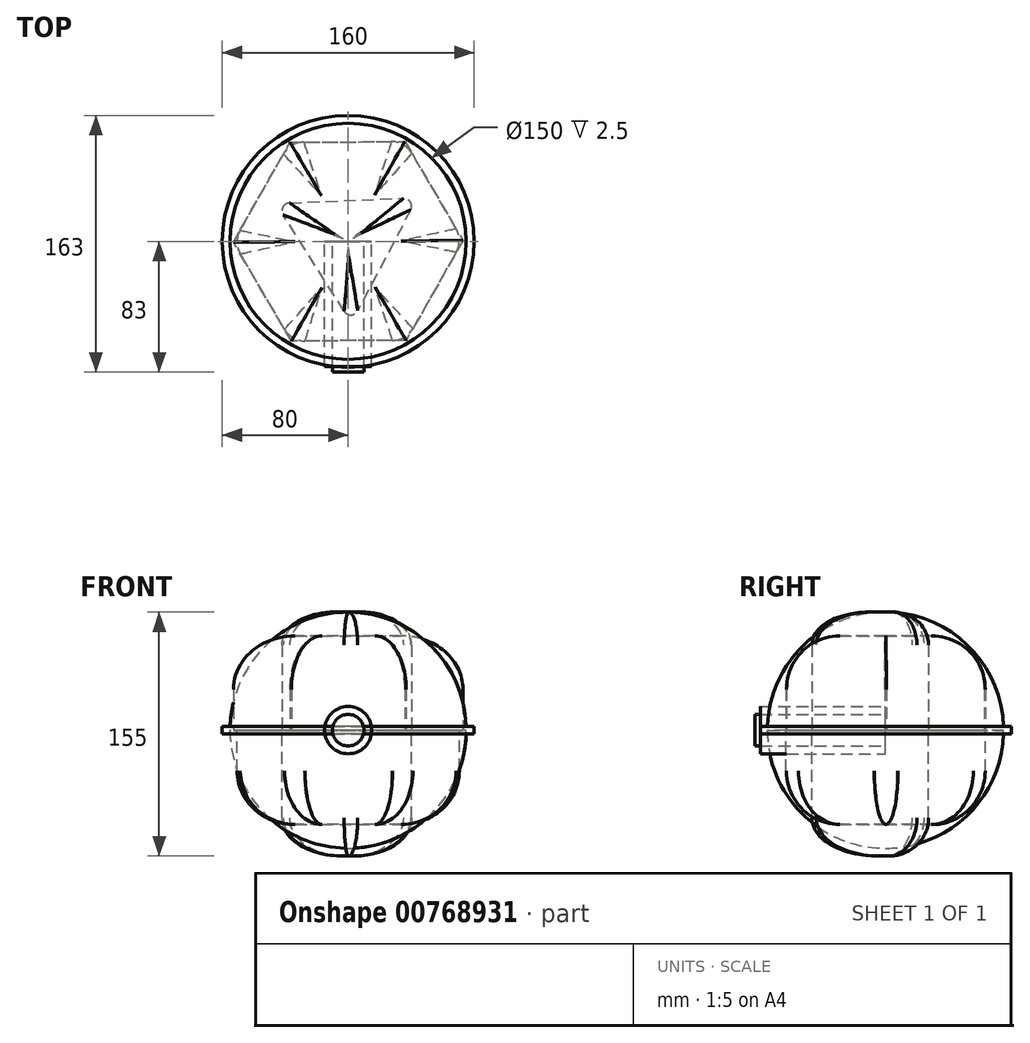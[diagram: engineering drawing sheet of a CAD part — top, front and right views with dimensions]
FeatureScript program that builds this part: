
annotation { "Feature Type Name" : "Feature", "Feature Type Description" : "" }
export const myFeature = defineFeature(function(context is Context, id is Id, definition is map)
    precondition{}
    {
        {
            var Q0;
            Q0=qCreatedBy(makeId("Top.planeOp"),FACE);
            var sketch = newSketch(context, id + "F0", { "sketchPlane" : qUnion([Q0])});
            skCircle(sketch, "E0", {"center": v(0, 0) * mm, "radius": 75 * mm});
            skSolve(sketch);
        }
        {
            var Q0;
            Q0=makeQuery(id+"F0.imprint","IMPRINT",FACE,{"disambiguationData":[TD([[makeQuery(id+"F0.imprint","IMPRINT",EDGE,{"derivedFrom":sQuery(id+"F0.wireOp",EDGE,"E0")}),1.0]])]});
            extrude(context, id + "F1", {"entities" : qUnion([Q0]), "depth" : 75 * mm, "offsetDistance" : 25 * mm});
        }
        {
            var Q0;
            Q0=makeQuery(id+"F1.opExtrude","CAP_FACE",FACE,{"disambiguationData":[OSD([sQuery(id+"F0.wireOp",EDGE,"E0")])],"isStart":true});
            extrude(context, id + "F2", {"entities" : qUnion([Q0]), "operationType" : NewBodyOperationType.ADD, "depth" : 75 * mm, "offsetDistance" : 25 * mm});
        }
        {
            var Q0;
            Q0=makeQuery(id+"F1.opExtrude","CAP_FACE",FACE,{"disambiguationData":[OSD([sQuery(id+"F0.wireOp",EDGE,"E0")])],"isStart":false});
            fillet(context, id + "F3", {"entities" : qUnion([Q0]), "radius" : 75 * mm, "tangentPropagation" : true, "allowEdgeOverflow" : false});
        }
        {
            var Q0;
            Q0=makeQuery(id+"F2.opExtrude","CAP_FACE",FACE,{"disambiguationData":[OSD([sQuery(id+"F0.wireOp",EDGE,"E0")])],"isStart":false});
            fillet(context, id + "F4", {"entities" : qUnion([Q0]), "radius" : 75 * mm, "tangentPropagation" : true, "allowEdgeOverflow" : false});
        }
        {
            var Q0;
            Q0=qCreatedBy(makeId("Top.planeOp"),FACE);
            var sketch = newSketch(context, id + "F5", { "sketchPlane" : qUnion([Q0])});
            skCircle(sketch, "E1", {"center": v(0, 0) * mm, "radius": 80 * mm});
            skSolve(sketch);
        }
        {
            var Q0;
            Q0=makeQuery(id+"F5.imprint","IMPRINT",FACE,{"disambiguationData":[TD([[makeQuery(id+"F5.imprint","IMPRINT",EDGE,{"derivedFrom":sQuery(id+"F5.wireOp",EDGE,"E1")}),1.0]])]});
            extrude(context, id + "F6", {"entities" : qUnion([Q0]), "operationType" : NewBodyOperationType.ADD, "depth" : 2.5 * mm, "offsetDistance" : 25 * mm});
        }
        {
            var Q0;
            Q0=makeQuery(id+"F6.opExtrude","CAP_FACE",FACE,{"disambiguationData":[OSD([sQuery(id+"F5.wireOp",EDGE,"E1")])],"isStart":true});
            extrude(context, id + "F7", {"entities" : qUnion([Q0]), "operationType" : NewBodyOperationType.ADD, "depth" : 2.5 * mm, "offsetDistance" : 25 * mm});
        }
        {
            var Q0;
            Q0=qCreatedBy(makeId("Front.planeOp"),FACE);
            var sketch = newSketch(context, id + "F8", { "sketchPlane" : qUnion([Q0])});
            skCircle(sketch, "E2", {"center": v(0, 0) * mm, "radius": 15 * mm});
            skSolve(sketch);
        }
        {
            var Q0;
            Q0=sQuery(id+"F8.wireOp",EDGE,"E2");
            extrude(context, id + "F9", {"bodyType" : ToolBodyType.SURFACE, "surfaceEntities" : qUnion([Q0]), "depth" : 78.5 * mm, "offsetDistance" : 25 * mm});
        }
        {
            var Q0;
            Q0=qCreatedBy(makeId("Front.planeOp"),FACE);
            var sketch = newSketch(context, id + "F10", { "sketchPlane" : qUnion([Q0])});
            skCircle(sketch, "E3", {"center": v(0, 0) * mm, "radius": 10 * mm});
            skSolve(sketch);
        }
        {
            var Q0;
            Q0=sQuery(id+"F10.wireOp",EDGE,"E3");
            extrude(context, id + "F11", {"bodyType" : ToolBodyType.SURFACE, "surfaceEntities" : qUnion([Q0]), "depth" : 83 * mm, "offsetDistance" : 25 * mm});
        }
        {
            var Q0;
            Q0 = qSketchRegion(id + "F10", true);
            extrude(context, id + "F12", {"entities" : qUnion([Q0]), "depth" : 83 * mm, "offsetDistance" : 25 * mm});
        }
        {
            var Q0;
            Q0 = qSketchRegion(id + "F8", true);
            extrude(context, id + "F13", {"entities" : qUnion([Q0]), "depth" : 79.5 * mm, "offsetDistance" : 25 * mm});
        }
        {
            var Q0;
            Q0=qCreatedBy(makeId("Top.planeOp"),FACE);
            var sketch = newSketch(context, id + "F14", { "sketchPlane" : qUnion([Q0])});
            skCircle(sketch, "E4.cCircle", {"center": v(0, 0) * mm, "radius": 25.89 * mm, "construction": true});
            skLineSegment(sketch, "E4.0", {"start": v(43.76, 27.68) * mm, "end": v(2.1, -51.73) * mm});
            skLineSegment(sketch, "E4.1", {"start": v(2.1, -51.73) * mm, "end": v(-45.85, 24.06) * mm});
            skLineSegment(sketch, "E4.2", {"start": v(-45.85, 24.06) * mm, "end": v(43.76, 27.68) * mm});
            skPoint(sketch, "E4.0.midPoint", {"position": v(22.92, -12.03) * mm});
            skSolve(sketch);
        }
        {
            var Q0;
            Q0 = qSketchRegion(id + "F14", true);
            extrude(context, id + "F15", {"entities" : qUnion([Q0]), "depth" : 75 * mm, "offsetDistance" : 25 * mm});
        }
        {
            var Q0;
            Q0=makeQuery(id+"F15.opExtrude","SWEPT_EDGE",EDGE,{"disambiguationData":[OSD([sQuery(id+"F14.wireOp",EDGE,"E4.0"),sQuery(id+"F14.wireOp",EDGE,"E4.1")])]});
            var Q1;
            Q1=makeQuery(id+"F15.opExtrude","SWEPT_EDGE",EDGE,{"disambiguationData":[OSD([sQuery(id+"F14.wireOp",EDGE,"E4.0"),sQuery(id+"F14.wireOp",EDGE,"E4.2")])]});
            var Q2;
            Q2=makeQuery(id+"F15.opExtrude","SWEPT_EDGE",EDGE,{"disambiguationData":[OSD([sQuery(id+"F14.wireOp",EDGE,"E4.1"),sQuery(id+"F14.wireOp",EDGE,"E4.2")])]});
            fillet(context, id + "F16", {"entities" : qUnion([Q0, Q1, Q2]), "radius" : 5 * mm, "tangentPropagation" : true, "allowEdgeOverflow" : false});
        }
        {
            var Q0;
            Q0=makeQuery(id+"F15.opExtrude","CAP_FACE",FACE,{"disambiguationData":[OSD([sQuery(id+"F14.wireOp",EDGE,"E4.0"),sQuery(id+"F14.wireOp",EDGE,"E4.1"),sQuery(id+"F14.wireOp",EDGE,"E4.2")])],"isStart":false});
            fillet(context, id + "F17", {"entities" : qUnion([Q0]), "radius" : 21 * mm, "tangentPropagation" : true, "allowEdgeOverflow" : false});
        }
        {
            var Q0;
            Q0 = qSketchRegion(id + "F14", true);
            extrude(context, id + "F18", {"entities" : qUnion([Q0]), "oppositeDirection" : true, "depth" : 80 * mm, "offsetDistance" : 25 * mm});
        }
        {
            var Q0;
            Q0=makeQuery(id+"F18.opExtrude","SWEPT_EDGE",EDGE,{"disambiguationData":[OSD([sQuery(id+"F14.wireOp",EDGE,"E4.1"),sQuery(id+"F14.wireOp",EDGE,"E4.2")])]});
            var Q1;
            Q1=makeQuery(id+"F18.opExtrude","SWEPT_EDGE",EDGE,{"disambiguationData":[OSD([sQuery(id+"F14.wireOp",EDGE,"E4.0"),sQuery(id+"F14.wireOp",EDGE,"E4.2")])]});
            var Q2;
            Q2=makeQuery(id+"F18.opExtrude","SWEPT_EDGE",EDGE,{"disambiguationData":[OSD([sQuery(id+"F14.wireOp",EDGE,"E4.0"),sQuery(id+"F14.wireOp",EDGE,"E4.1")])]});
            fillet(context, id + "F19", {"entities" : qUnion([Q0, Q1, Q2]), "radius" : 5 * mm, "tangentPropagation" : true, "allowEdgeOverflow" : false});
        }
        {
            var Q0;
            Q0=makeQuery(id+"F18.opExtrude","CAP_FACE",FACE,{"disambiguationData":[OSD([sQuery(id+"F14.wireOp",EDGE,"E4.0"),sQuery(id+"F14.wireOp",EDGE,"E4.1"),sQuery(id+"F14.wireOp",EDGE,"E4.2")])],"isStart":false});
            fillet(context, id + "F20", {"entities" : qUnion([Q0]), "radius" : 24.14 * mm, "tangentPropagation" : true, "allowEdgeOverflow" : false});
        }
        {
            var Q0;
            Q0=qCreatedBy(makeId("Top.planeOp"),FACE);
            var sketch = newSketch(context, id + "F21", { "sketchPlane" : qUnion([Q0])});
            skCircle(sketch, "E5.cCircle", {"center": v(0, 0) * mm, "radius": 63.14 * mm, "construction": true});
            skLineSegment(sketch, "E5.0", {"start": v(36.04, 63.37) * mm, "end": v(72.9, 0.48) * mm});
            skLineSegment(sketch, "E5.1", {"start": v(72.9, 0.48) * mm, "end": v(36.86, -62.9) * mm});
            skLineSegment(sketch, "E5.2", {"start": v(36.86, -62.9) * mm, "end": v(-36.04, -63.37) * mm});
            skLineSegment(sketch, "E5.3", {"start": v(-36.04, -63.37) * mm, "end": v(-72.9, -0.48) * mm});
            skLineSegment(sketch, "E5.4", {"start": v(-72.9, -0.48) * mm, "end": v(-36.86, 62.9) * mm});
            skLineSegment(sketch, "E5.5", {"start": v(-36.86, 62.9) * mm, "end": v(36.04, 63.37) * mm});
            skPoint(sketch, "E5.0.midPoint", {"position": v(54.47, 31.93) * mm});
            skSolve(sketch);
        }
        {
            var Q0;
            Q0 = qSketchRegion(id + "F21", true);
            extrude(context, id + "F22", {"entities" : qUnion([Q0]), "oppositeDirection" : true, "depth" : 60 * mm, "offsetDistance" : 25 * mm});
        }
        {
            var Q0;
            Q0 = qSketchRegion(id + "F21", true);
            extrude(context, id + "F23", {"entities" : qUnion([Q0]), "depth" : 60 * mm, "offsetDistance" : 25 * mm});
        }
        {
            var Q0;
            Q0=makeQuery(id+"F22.opExtrude","SWEPT_EDGE",EDGE,{"disambiguationData":[OSD([sQuery(id+"F21.wireOp",EDGE,"E5.1"),sQuery(id+"F21.wireOp",EDGE,"E5.2")])]});
            var Q1;
            Q1=makeQuery(id+"F22.opExtrude","SWEPT_EDGE",EDGE,{"disambiguationData":[OSD([sQuery(id+"F21.wireOp",EDGE,"E5.0"),sQuery(id+"F21.wireOp",EDGE,"E5.1")])]});
            var Q2;
            Q2=makeQuery(id+"F22.opExtrude","SWEPT_EDGE",EDGE,{"disambiguationData":[OSD([sQuery(id+"F21.wireOp",EDGE,"E5.4"),sQuery(id+"F21.wireOp",EDGE,"E5.5")])]});
            var Q3;
            Q3=makeQuery(id+"F22.opExtrude","SWEPT_EDGE",EDGE,{"disambiguationData":[OSD([sQuery(id+"F21.wireOp",EDGE,"E5.3"),sQuery(id+"F21.wireOp",EDGE,"E5.4")])]});
            var Q4;
            Q4=makeQuery(id+"F22.opExtrude","SWEPT_EDGE",EDGE,{"disambiguationData":[OSD([sQuery(id+"F21.wireOp",EDGE,"E5.2"),sQuery(id+"F21.wireOp",EDGE,"E5.3")])]});
            var Q5;
            Q5=makeQuery(id+"F22.opExtrude","SWEPT_EDGE",EDGE,{"disambiguationData":[OSD([sQuery(id+"F21.wireOp",EDGE,"E5.0"),sQuery(id+"F21.wireOp",EDGE,"E5.5")])]});
            fillet(context, id + "F24", {"entities" : qUnion([Q0, Q1, Q2, Q3, Q4, Q5]), "radius" : 15 * mm, "tangentPropagation" : true, "allowEdgeOverflow" : false});
        }
        {
            var Q0;
            Q0=makeQuery(id+"F22.opExtrude","CAP_FACE",FACE,{"disambiguationData":[OSD([sQuery(id+"F21.wireOp",EDGE,"E5.0"),sQuery(id+"F21.wireOp",EDGE,"E5.1"),sQuery(id+"F21.wireOp",EDGE,"E5.2"),sQuery(id+"F21.wireOp",EDGE,"E5.3"),sQuery(id+"F21.wireOp",EDGE,"E5.4"),sQuery(id+"F21.wireOp",EDGE,"E5.5")])],"isStart":false});
            fillet(context, id + "F25", {"entities" : qUnion([Q0]), "radius" : 34 * mm, "tangentPropagation" : true, "allowEdgeOverflow" : false});
        }
        {
            var Q0;
            Q0=makeQuery(id+"F23.opExtrude","CAP_FACE",FACE,{"disambiguationData":[OSD([sQuery(id+"F21.wireOp",EDGE,"E5.0"),sQuery(id+"F21.wireOp",EDGE,"E5.1"),sQuery(id+"F21.wireOp",EDGE,"E5.2"),sQuery(id+"F21.wireOp",EDGE,"E5.3"),sQuery(id+"F21.wireOp",EDGE,"E5.4"),sQuery(id+"F21.wireOp",EDGE,"E5.5")])],"isStart":false});
            fillet(context, id + "F26", {"entities" : qUnion([Q0]), "radius" : 34 * mm, "tangentPropagation" : true, "allowEdgeOverflow" : false});
        }
    });
